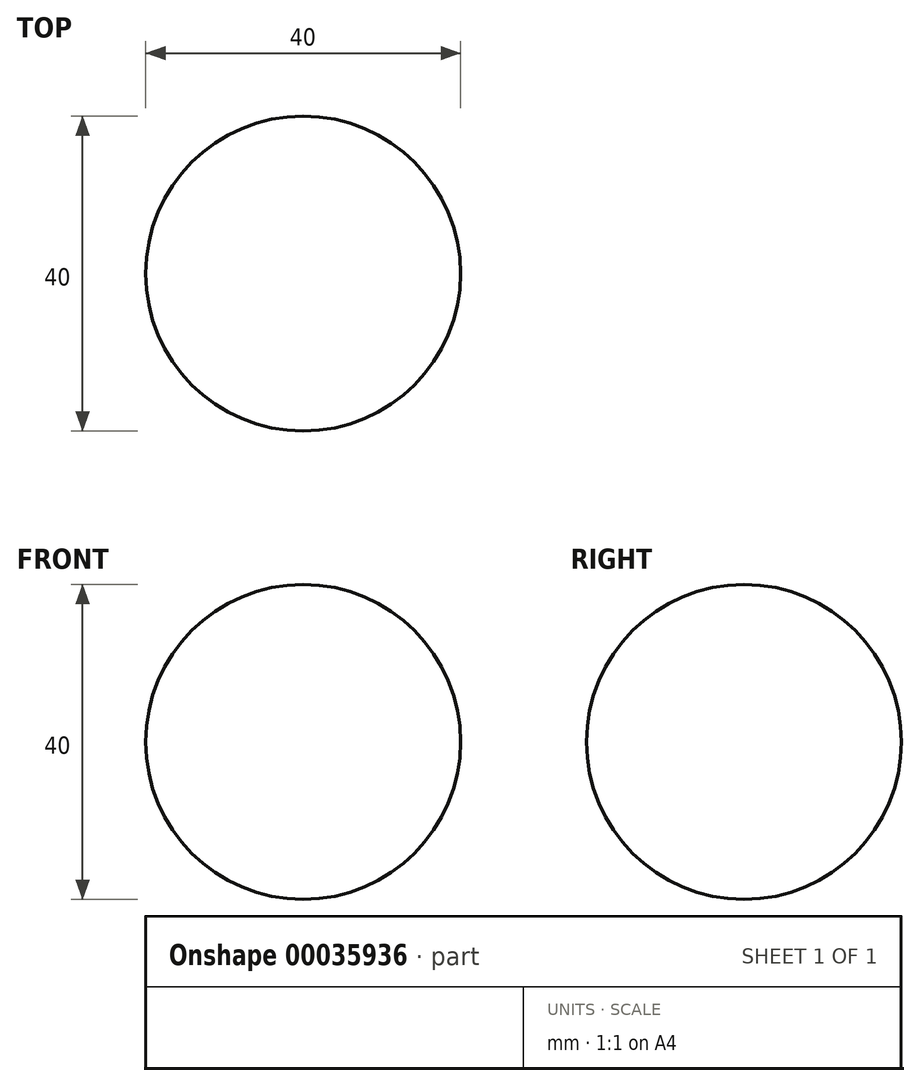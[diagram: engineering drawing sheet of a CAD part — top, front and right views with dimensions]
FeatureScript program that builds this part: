
annotation { "Feature Type Name" : "Feature", "Feature Type Description" : "" }
export const myFeature = defineFeature(function(context is Context, id is Id, definition is map)
    precondition{}
    {
        {
            var Q0;
            Q0=qCreatedBy(makeId("Front.planeOp"),FACE);
            var sketch = newSketch(context, id + "F0", { "sketchPlane" : qUnion([Q0])});
            skArc(sketch, "E0", {"start": v(-20, 0) * mm, "mid": v(0, -20) * mm, "end": v(20, 0) * mm});
            skLineSegment(sketch, "E1", {"start": v(-20, 0) * mm, "end": v(20, 0) * mm});
            skSolve(sketch);
        }
        {
            var Q0;
            Q0 = qSketchRegion(id + "F0", true);
            var Q1;
            Q1=sQuery(id+"F0.wireOp",EDGE,"E1");
            revolve(context, id + "F1", {"entities" : qUnion([Q0]), "axis" : qUnion([Q1]), "revolveType" : RevolveType.FULL});
        }
    });
